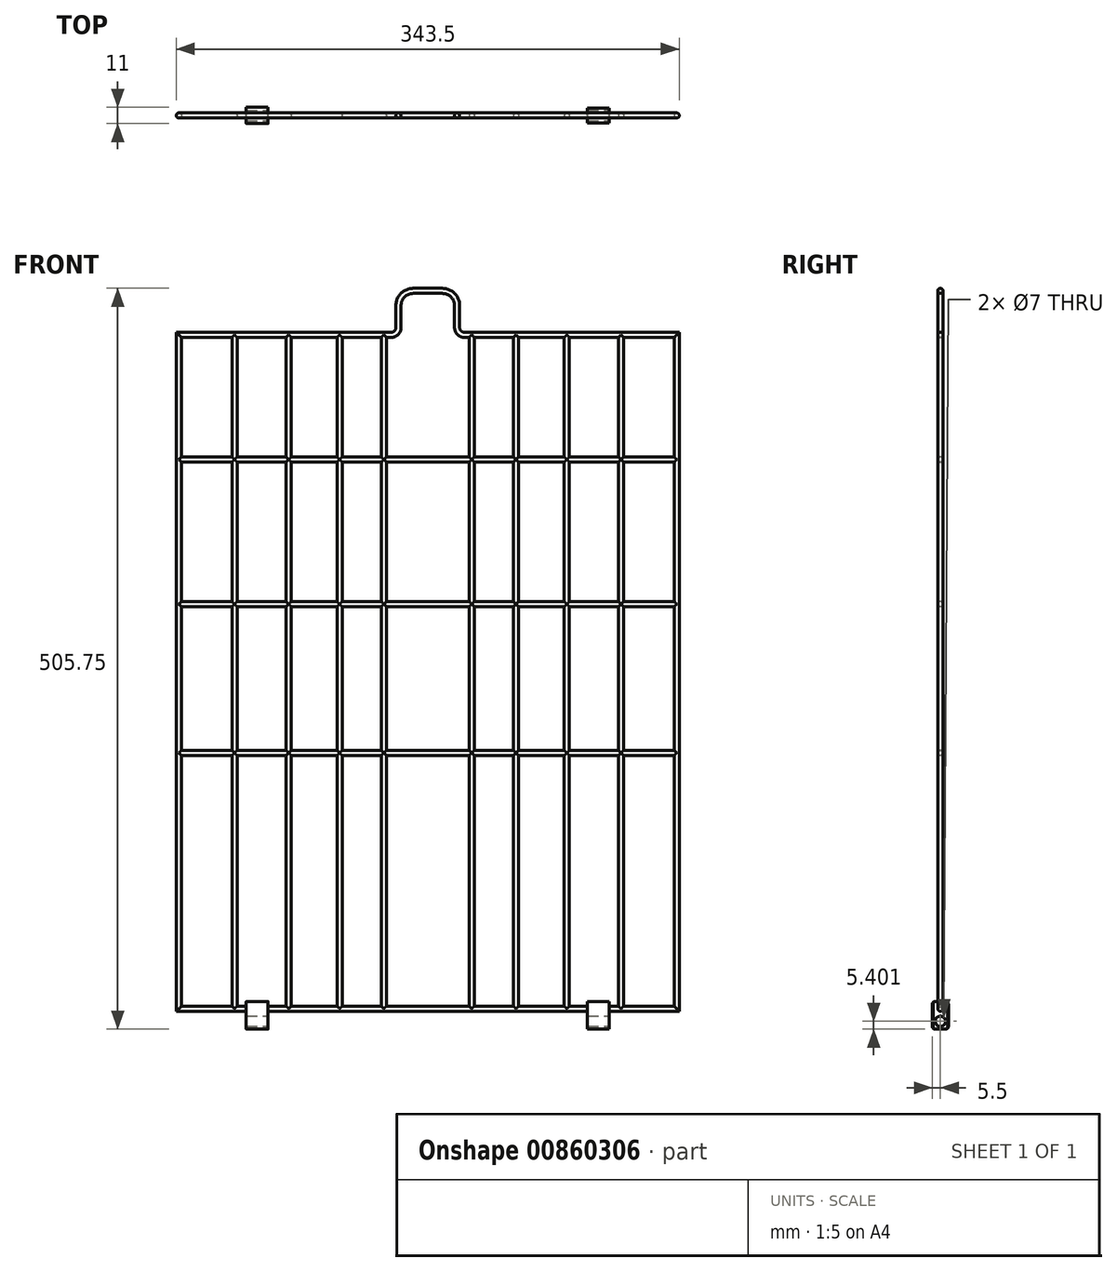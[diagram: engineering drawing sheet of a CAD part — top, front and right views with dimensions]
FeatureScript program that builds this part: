
annotation { "Feature Type Name" : "Feature", "Feature Type Description" : "" }
export const myFeature = defineFeature(function(context is Context, id is Id, definition is map)
    precondition{}
    {
        {
            var Q0;
            Q0=qCreatedBy(makeId("Front.planeOp"),FACE);
            var sketch = newSketch(context, id + "F0", { "sketchPlane" : qUnion([Q0])});
            skLineSegment(sketch, "E0", {"start": v(-150, 0) * mm, "end": v(-5, 0) * mm});
            skLineSegment(sketch, "E1", {"start": v(0, 5) * mm, "end": v(0, 20) * mm});
            skLineSegment(sketch, "E2", {"start": v(10, 30) * mm, "end": v(20, 30) * mm});
            skPoint(sketch, "E3.visualSharp", {"position": v(0, 30) * mm});
            skArc(sketch, "E3.filletArc", {"start": v(10, 30) * mm, "mid": v(2.93, 27.07) * mm, "end": v(0, 20) * mm});
            skPoint(sketch, "E4.visualSharp", {"position": v(0, 0) * mm});
            skArc(sketch, "E4.filletArc", {"start": v(-5, 0) * mm, "mid": v(-1.46, 1.46) * mm, "end": v(0, 5) * mm});
            skLineSegment(sketch, "E5", {"start": v(20, 30) * mm, "end": v(20, -13.15) * mm});
            skArc(sketch, "E6.MirrorCS", {"start": v(30, 30) * mm, "mid": v(37.07, 27.07) * mm, "end": v(40, 20) * mm});
            skLineSegment(sketch, "E7.MirrorCS", {"start": v(30, 30) * mm, "end": v(20, 30) * mm});
            skLineSegment(sketch, "E8.MirrorCS", {"start": v(40, 5) * mm, "end": v(40, 20) * mm});
            skArc(sketch, "E9.MirrorCS", {"start": v(45, 0) * mm, "mid": v(41.46, 1.46) * mm, "end": v(40, 5) * mm});
            skLineSegment(sketch, "E10.MirrorCS", {"start": v(190, 0) * mm, "end": v(45, 0) * mm});
            skLineSegment(sketch, "E11", {"start": v(-150, 0) * mm, "end": v(-150, -460) * mm});
            skLineSegment(sketch, "E12", {"start": v(190, 0) * mm, "end": v(190, -460) * mm});
            skLineSegment(sketch, "E13", {"start": v(-75, 0) * mm, "end": v(-75, -460) * mm});
            skLineSegment(sketch, "E14", {"start": v(-10, 0) * mm, "end": v(-10, -460) * mm});
            skLineSegment(sketch, "E15", {"start": v(-150, -460) * mm, "end": v(190, -460) * mm});
            skLineSegment(sketch, "E16", {"start": v(-111.94, 0) * mm, "end": v(-111.94, -460) * mm});
            skLineSegment(sketch, "E17", {"start": v(-40.24, 0) * mm, "end": v(-40.24, -460) * mm});
            skLineSegment(sketch, "E18", {"start": v(-150, -285.4) * mm, "end": v(190, -285.4) * mm});
            skLineSegment(sketch, "E19", {"start": v(-150, -183.78) * mm, "end": v(190, -183.78) * mm});
            skLineSegment(sketch, "E20", {"start": v(-150, -85.14) * mm, "end": v(190, -85.14) * mm});
            skLineSegment(sketch, "E21.bottom", {"start": v(-104, -455) * mm, "end": v(-89, -455) * mm});
            skLineSegment(sketch, "E21.top", {"start": v(-104, -474) * mm, "end": v(-89, -474) * mm});
            skLineSegment(sketch, "E21.left", {"start": v(-104, -455) * mm, "end": v(-104, -474) * mm});
            skLineSegment(sketch, "E21.right", {"start": v(-89, -455) * mm, "end": v(-89, -474) * mm});
            skLineSegment(sketch, "E22.bottom", {"start": v(129, -455) * mm, "end": v(144, -455) * mm});
            skLineSegment(sketch, "E22.top", {"start": v(129, -474) * mm, "end": v(144, -474) * mm});
            skLineSegment(sketch, "E22.left", {"start": v(129, -455) * mm, "end": v(129, -474) * mm});
            skLineSegment(sketch, "E22.right", {"start": v(144, -455) * mm, "end": v(144, -474) * mm});
            skSolve(sketch);
        }
        {
            var Q0;
            Q0=qCreatedBy(makeId("Right.planeOp"),FACE);
            cPlane(context, id + "F1", {"entities" : qUnion([Q0]), "cplaneType" : CPlaneType.OFFSET, "offset" : 190 * mm, "width" : 150 * mm, "height" : 150 * mm});
        }
        {
            var Q0;
            Q0=qCreatedBy(id+"F1.planeOp",FACE);
            var sketch = newSketch(context, id + "F2", { "sketchPlane" : qUnion([Q0])});
            skCircle(sketch, "E23", {"center": v(0, 0) * mm, "radius": 1.75 * mm});
            skSolve(sketch);
        }
        {
            var Q0;
            Q0=makeQuery(id+"F2.imprint","IMPRINT",FACE,{"disambiguationData":[TD([[makeQuery(id+"F2.imprint","IMPRINT",EDGE,{"derivedFrom":sQuery(id+"F2.wireOp",EDGE,"E23")}),1.0]])]});
            var Q1;
            Q1=sQuery(id+"F0.wireOp",EDGE,"E10.MirrorCS");
            var Q2;
            Q2=sQuery(id+"F0.wireOp",EDGE,"E9.MirrorCS");
            var Q3;
            Q3=sQuery(id+"F0.wireOp",EDGE,"E8.MirrorCS");
            var Q4;
            Q4=sQuery(id+"F0.wireOp",EDGE,"E6.MirrorCS");
            var Q5;
            Q5=sQuery(id+"F0.wireOp",EDGE,"E7.MirrorCS");
            var Q6;
            Q6=sQuery(id+"F0.wireOp",EDGE,"E2");
            var Q7;
            Q7=sQuery(id+"F0.wireOp",EDGE,"E3.filletArc");
            var Q8;
            Q8=sQuery(id+"F0.wireOp",EDGE,"E1");
            var Q9;
            Q9=sQuery(id+"F0.wireOp",EDGE,"E4.filletArc");
            var Q10;
            Q10=sQuery(id+"F0.wireOp",EDGE,"E0");
            var Q11;
            Q11=sQuery(id+"F0.wireOp",EDGE,"E11");
            var Q12;
            Q12=sQuery(id+"F0.wireOp",EDGE,"E12");
            var Q13;
            Q13=sQuery(id+"F0.wireOp",EDGE,"E15");
            sweep(context, id + "F3", {"profiles" : qUnion([Q0]), "path" : qUnion([Q1, Q2, Q3, Q4, Q5, Q6, Q7, Q8, Q9, Q10, Q11, Q12, Q13])});
        }
        {
            var Q0;
            Q0=qCreatedBy(makeId("Top.planeOp"),FACE);
            var sketch = newSketch(context, id + "F4", { "sketchPlane" : qUnion([Q0])});
            skCircle(sketch, "E24", {"center": v(0, 0) * mm, "radius": 1.75 * mm});
            skCircle(sketch, "E25", {"center": v(-74.98, 0) * mm, "radius": 1.75 * mm});
            skSolve(sketch);
        }
        {
            var Q0;
            Q0=makeQuery(id+"F4.imprint","IMPRINT",FACE,{"disambiguationData":[TD([[makeQuery(id+"F4.imprint","IMPRINT",EDGE,{"derivedFrom":sQuery(id+"F4.wireOp",EDGE,"E25")}),1.0]])]});
            var Q1;
            Q1=sQuery(id+"F0.wireOp",EDGE,"E13");
            sweep(context, id + "F5", {"profiles" : qUnion([Q0]), "path" : qUnion([Q1])});
        }
        {
            var Q0;
            Q0=qCreatedBy(makeId("Top.planeOp"),FACE);
            var sketch = newSketch(context, id + "F6", { "sketchPlane" : qUnion([Q0])});
            skCircle(sketch, "E26", {"center": v(-10, 0) * mm, "radius": 1.75 * mm});
            skSolve(sketch);
        }
        {
            var Q0;
            Q0=qSketchRegion(id+"F6",true);
            var Q1;
            Q1=sQuery(id+"F0.wireOp",EDGE,"E14");
            sweep(context, id + "F7", {"profiles" : qUnion([Q0]), "path" : qUnion([Q1])});
        }
        {
            var Q0;
            Q0=qCreatedBy(makeId("Right.planeOp"),FACE);
            cPlane(context, id + "F8", {"entities" : qUnion([Q0]), "cplaneType" : CPlaneType.OFFSET, "offset" : 20 * mm, "width" : 150 * mm, "height" : 150 * mm});
        }
        {
            var Q0;
            Q0=makeQuery(id+"F5.opSweep","SWEPT_BODY",BODY,{"disambiguationData":[OSD([sQuery(id+"F0.wireOp",EDGE,"E13"),sQuery(id+"F4.wireOp",EDGE,"E25")])]});
            var Q1;
            Q1=makeQuery(id+"F7.opSweep","SWEPT_BODY",BODY,{"disambiguationData":[OSD([sQuery(id+"F0.wireOp",EDGE,"E14"),sQuery(id+"F6.wireOp",EDGE,"E26")])]});
            var Q2;
            Q2=qCreatedBy(id+"F8.planeOp",FACE);
            mirror(context, id + "F9", {"operationType" : NewBodyOperationType.ADD, "entities" : qUnion([Q0, Q1]), "mirrorPlane" : qUnion([Q2])});
        }
        {
            var Q0;
            Q0=qCreatedBy(makeId("Top.planeOp"),FACE);
            var sketch = newSketch(context, id + "F10", { "sketchPlane" : qUnion([Q0])});
            skCircle(sketch, "E27", {"center": v(-111.94, 0) * mm, "radius": 1.75 * mm});
            skCircle(sketch, "E28", {"center": v(-40.24, 0) * mm, "radius": 1.75 * mm});
            skSolve(sketch);
        }
        {
            var Q0;
            Q0=qSketchRegion(id+"F10",true);
            var Q1;
            Q1=sQuery(id+"F0.wireOp",EDGE,"E16");
            sweep(context, id + "F11", {"profiles" : qUnion([Q0]), "path" : qUnion([Q1])});
        }
        {
            var Q0;
            Q0=makeQuery(id+"F11.opSweep","SWEPT_BODY",BODY,{"disambiguationData":[OSD([sQuery(id+"F0.wireOp",EDGE,"E16"),sQuery(id+"F10.wireOp",EDGE,"E27")])]});
            var Q1;
            Q1=makeQuery(id+"F11.opSweep","SWEPT_BODY",BODY,{"disambiguationData":[OSD([sQuery(id+"F0.wireOp",EDGE,"E16"),sQuery(id+"F10.wireOp",EDGE,"E28")])]});
            var Q2;
            Q2=qCreatedBy(id+"F8.planeOp",FACE);
            mirror(context, id + "F12", {"operationType" : NewBodyOperationType.ADD, "entities" : qUnion([Q0, Q1]), "mirrorPlane" : qUnion([Q2])});
        }
        {
            var Q0;
            Q0=qCreatedBy(id+"F1.planeOp",FACE);
            var sketch = newSketch(context, id + "F13", { "sketchPlane" : qUnion([Q0])});
            skCircle(sketch, "E29", {"center": v(0, -285.4) * mm, "radius": 1.75 * mm});
            skSolve(sketch);
        }
        {
            var Q0;
            Q0=qSketchRegion(id+"F13",true);
            var Q1;
            Q1=sQuery(id+"F0.wireOp",EDGE,"E18");
            sweep(context, id + "F14", {"operationType" : NewBodyOperationType.ADD, "profiles" : qUnion([Q0]), "path" : qUnion([Q1])});
        }
        {
            var Q0;
            Q0=qCreatedBy(id+"F1.planeOp",FACE);
            var sketch = newSketch(context, id + "F15", { "sketchPlane" : qUnion([Q0])});
            skCircle(sketch, "E30", {"center": v(0, -85.14) * mm, "radius": 1.75 * mm});
            skCircle(sketch, "E31", {"center": v(0, -183.83) * mm, "radius": 1.75 * mm});
            skSolve(sketch);
        }
        {
            var Q0;
            Q0=qSketchRegion(id+"F15",true);
            var Q1;
            Q1=sQuery(id+"F0.wireOp",EDGE,"E19");
            sweep(context, id + "F16", {"operationType" : NewBodyOperationType.ADD, "profiles" : qUnion([Q0]), "path" : qUnion([Q1])});
        }
        {
            var Q0;
            {var subQ5=sQuery(id+"F0.wireOp",EDGE,"E21.top");Q0=makeQuery(id+"F0.imprint","IMPRINT",FACE,{"disambiguationData":[TD([[makeQuery(id+"F0.imprint","IMPRINT",EDGE,{"derivedFrom":subQ5}),1.0]])]});}
            var Q1;
            {var subQ5=sQuery(id+"F0.wireOp",EDGE,"E21.bottom");Q1=makeQuery(id+"F0.imprint","IMPRINT",FACE,{"disambiguationData":[TD([[makeQuery(id+"F0.imprint","IMPRINT",EDGE,{"derivedFrom":subQ5}),-1.0]])]});}
            extrude(context, id + "F17", {"entities" : qUnion([Q0, Q1]), "operationType" : NewBodyOperationType.ADD, "endBound" : BoundingType.SYMMETRIC, "depth" : 11 * mm, "offsetDistance" : 25 * mm});
        }
        {
            var Q0;
            Q0=makeQuery(id+"F17.opExtrude","CAP_EDGE",EDGE,{"disambiguationData":[OSD([sQuery(id+"F0.wireOp",EDGE,"E21.bottom")])],"isStart":false});
            var Q1;
            Q1=makeQuery(id+"F17.opExtrude","CAP_EDGE",EDGE,{"disambiguationData":[OSD([sQuery(id+"F0.wireOp",EDGE,"E21.top")])],"isStart":false});
            var Q2;
            Q2=makeQuery(id+"F17.opExtrude","CAP_EDGE",EDGE,{"disambiguationData":[OSD([sQuery(id+"F0.wireOp",EDGE,"E21.top")])],"isStart":true});
            var Q3;
            Q3=makeQuery(id+"F17.opExtrude","CAP_EDGE",EDGE,{"disambiguationData":[OSD([sQuery(id+"F0.wireOp",EDGE,"E21.bottom")])],"isStart":true});
            fillet(context, id + "F18", {"entities" : qUnion([Q0, Q1, Q2, Q3]), "radius" : 2 * mm, "tangentPropagation" : true, "allowEdgeOverflow" : false});
        }
        {
            var Q0;
            {var subQ5=sQuery(id+"F0.wireOp",EDGE,"E22.top");Q0=makeQuery(id+"F0.imprint","IMPRINT",FACE,{"disambiguationData":[TD([[makeQuery(id+"F0.imprint","IMPRINT",EDGE,{"derivedFrom":subQ5}),1.0]])]});}
            var Q1;
            {var subQ5=sQuery(id+"F0.wireOp",EDGE,"E22.bottom");Q1=makeQuery(id+"F0.imprint","IMPRINT",FACE,{"disambiguationData":[TD([[makeQuery(id+"F0.imprint","IMPRINT",EDGE,{"derivedFrom":subQ5}),-1.0]])]});}
            extrude(context, id + "F19", {"entities" : qUnion([Q0, Q1]), "operationType" : NewBodyOperationType.ADD, "endBound" : BoundingType.SYMMETRIC, "oppositeDirection" : true, "depth" : 10 * mm, "offsetDistance" : 25 * mm});
        }
        {
            var Q0;
            Q0=makeQuery(id+"F19.opExtrude","CAP_EDGE",EDGE,{"disambiguationData":[OSD([sQuery(id+"F0.wireOp",EDGE,"E22.bottom")])],"isStart":true});
            var Q1;
            Q1=makeQuery(id+"F19.opExtrude","CAP_EDGE",EDGE,{"disambiguationData":[OSD([sQuery(id+"F0.wireOp",EDGE,"E22.bottom")])],"isStart":false});
            var Q2;
            Q2=makeQuery(id+"F19.opExtrude","CAP_EDGE",EDGE,{"disambiguationData":[OSD([sQuery(id+"F0.wireOp",EDGE,"E22.top")])],"isStart":true});
            var Q3;
            Q3=makeQuery(id+"F19.opExtrude","CAP_EDGE",EDGE,{"disambiguationData":[OSD([sQuery(id+"F0.wireOp",EDGE,"E22.top")])],"isStart":false});
            fillet(context, id + "F20", {"entities" : qUnion([Q0, Q1, Q2, Q3]), "radius" : 2 * mm, "tangentPropagation" : true, "allowEdgeOverflow" : false});
        }
        {
            var Q0;
            Q0=makeQuery(id+"F19.opExtrude","SWEPT_FACE",FACE,{"disambiguationData":[OSD([sQuery(id+"F0.wireOp",EDGE,"E22.right")])]});
            var sketch = newSketch(context, id + "F21", { "sketchPlane" : qUnion([Q0])});
            skCircle(sketch, "E32", {"center": v(0, -468.6) * mm, "radius": 3.5 * mm});
            skSolve(sketch);
        }
        {
            var Q0;
            Q0=makeQuery(id+"F21.imprint","IMPRINT",FACE,{"disambiguationData":[TD([[makeQuery(id+"F21.imprint","IMPRINT",EDGE,{"derivedFrom":sQuery(id+"F21.wireOp",EDGE,"E32")}),1.0]])]});
            extrude(context, id + "F22", {"entities" : qUnion([Q0]), "operationType" : NewBodyOperationType.REMOVE, "oppositeDirection" : true, "depth" : 300 * mm, "offsetDistance" : 25 * mm});
        }
    });
